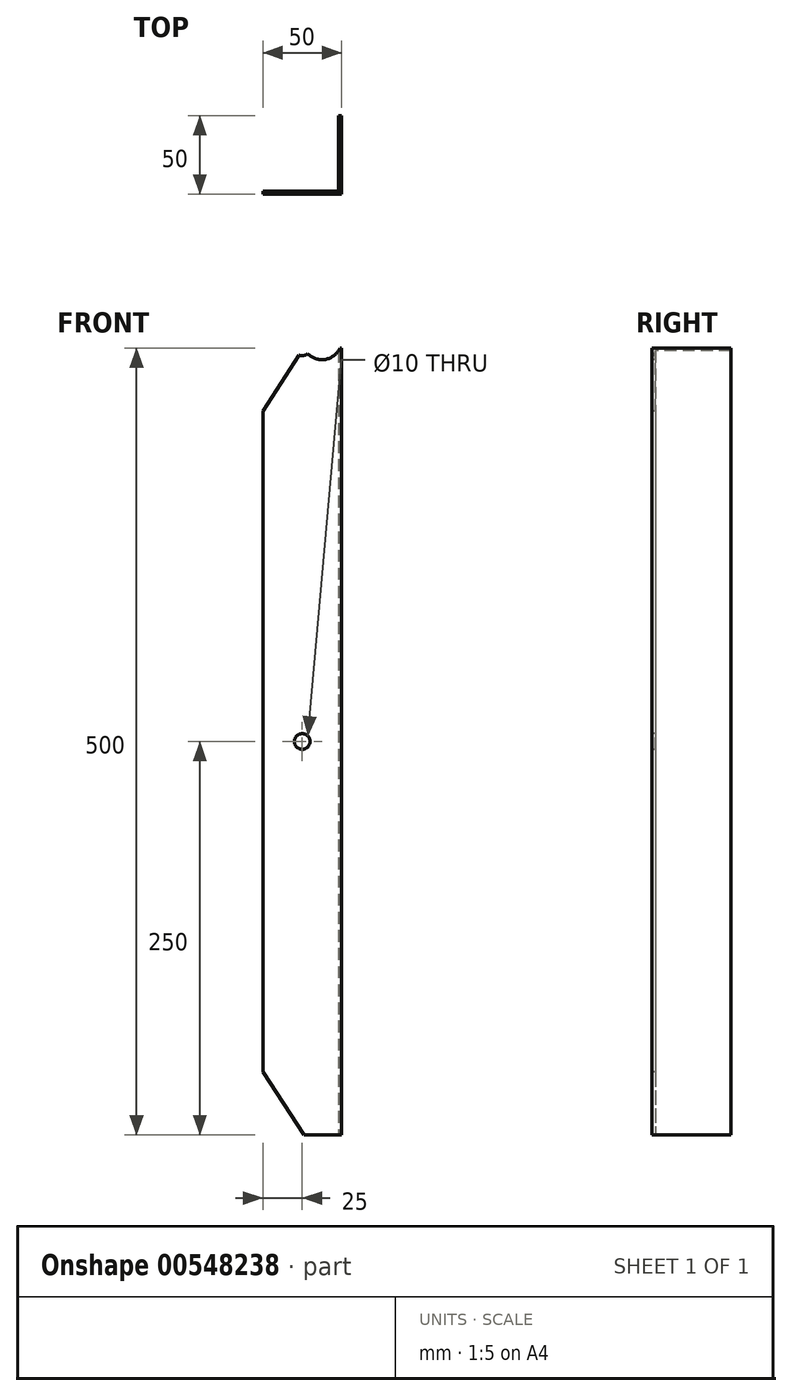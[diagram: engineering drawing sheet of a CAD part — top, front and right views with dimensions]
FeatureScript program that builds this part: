
annotation { "Feature Type Name" : "Feature", "Feature Type Description" : "" }
export const myFeature = defineFeature(function(context is Context, id is Id, definition is map)
    precondition{}
    {
        {
            var Q0;
            Q0=qCreatedBy(makeId("Top.planeOp"),FACE);
            var sketch = newSketch(context, id + "F0", { "sketchPlane" : qUnion([Q0])});
            skLineSegment(sketch, "E0", {"start": v(0, 0) * mm, "end": v(-50, 0) * mm});
            skLineSegment(sketch, "E1", {"start": v(0, 0) * mm, "end": v(0, 50) * mm});
            skLineSegment(sketch, "E2.0", {"start": v(-2, 2) * mm, "end": v(-50, 2) * mm});
            skLineSegment(sketch, "E2.1", {"start": v(-2, 2) * mm, "end": v(-2, 50) * mm});
            skLineSegment(sketch, "E3", {"start": v(-50, 2) * mm, "end": v(-50, 0) * mm});
            skLineSegment(sketch, "E4", {"start": v(-2, 50) * mm, "end": v(0, 50) * mm});
            skSolve(sketch);
        }
        {
            var Q0;
            Q0=makeQuery(id+"F0.imprint","IMPRINT",FACE,{"disambiguationData":[TD([[makeQuery(id+"F0.imprint","IMPRINT",EDGE,{"derivedFrom":sQuery(id+"F0.wireOp",EDGE,"E0")}),-1.0]])]});
            extrude(context, id + "F1", {"entities" : qUnion([Q0]), "depth" : 500 * mm, "offsetDistance" : 25 * mm});
        }
        {
            var Q0;
            Q0=makeQuery(id+"F1.opExtrude","SWEPT_FACE",FACE,{"disambiguationData":[OSD([sQuery(id+"F0.wireOp",EDGE,"E0")])]});
            var sketch = newSketch(context, id + "F2", { "sketchPlane" : qUnion([Q0])});
            skLineSegment(sketch, "E5", {"start": v(-25, 0) * mm, "end": v(-25, 500) * mm});
            skCircle(sketch, "E6", {"center": v(-25, 500) * mm, "radius": 5 * mm});
            skSolve(sketch);
        }
        {
            var Q0;
            Q0=makeQuery(id+"F2.imprint","IMPRINT",FACE,{"disambiguationData":[TD([[makeQuery(id+"F2.imprint","IMPRINT",EDGE,{"derivedFrom":sQuery(id+"F2.wireOp",EDGE,"E6")}),1.0]])]});
            extrude(context, id + "F3", {"entities" : qUnion([Q0]), "operationType" : NewBodyOperationType.REMOVE, "oppositeDirection" : true, "depth" : 25 * mm, "offsetDistance" : 25 * mm});
        }
        {
            var Q0;
            Q0=makeQuery(id+"F1.opExtrude","SWEPT_FACE",FACE,{"disambiguationData":[OSD([sQuery(id+"F0.wireOp",EDGE,"E0")])]});
            var sketch = newSketch(context, id + "F4", { "sketchPlane" : qUnion([Q0])});
            skLineSegment(sketch, "E7", {"start": v(0, 500) * mm, "end": v(-12.5, 500) * mm});
            skLineSegment(sketch, "E8", {"start": v(-12.5, 500) * mm, "end": v(-12.5, 505) * mm});
            skCircle(sketch, "E9", {"center": v(-12.5, 505) * mm, "radius": 12.5 * mm});
            skLineSegment(sketch, "E10", {"start": v(-50, 500) * mm, "end": v(-50, 460) * mm});
            skLineSegment(sketch, "E11", {"start": v(-50, 460) * mm, "end": v(-23.96, 500) * mm});
            skLineSegment(sketch, "E12", {"start": v(-23.96, 500) * mm, "end": v(-50, 500) * mm});
            skLineSegment(sketch, "E13", {"start": v(0, 250) * mm, "end": v(-50, 250) * mm});
            skLineSegment(sketch, "E14.MirrorCS", {"start": v(-50, 0) * mm, "end": v(-50, 40) * mm});
            skLineSegment(sketch, "E15.MirrorCS", {"start": v(-50, 40) * mm, "end": v(-23.96, 0) * mm});
            skLineSegment(sketch, "E16.MirrorCS", {"start": v(-23.96, 0) * mm, "end": v(-50, 0) * mm});
            skCircle(sketch, "E17.MirrorC", {"center": v(-12.5, -5) * mm, "radius": 12.5 * mm});
            skCircle(sketch, "E18", {"center": v(-25, 250) * mm, "radius": 5 * mm});
            skSolve(sketch);
        }
        {
            var Q0;
            {var subQ0=sQuery(id+"F4.wireOp",EDGE,"E7");var subQ1=makeQuery(id+"F1.opExtrude","CAP_EDGE",EDGE,{"disambiguationData":[OSD([sQuery(id+"F0.wireOp",EDGE,"E0")])],"isStart":false});var subQ2=makeQuery(id+"F4.imprint","INTERSECT",VERTEX,{"derivedFrom":[subQ1,subQ0]});Q0=makeQuery(id+"F4.imprint","IMPRINT",FACE,{"disambiguationData":[TD([[makeQuery(id+"F4.imprint","IMPRINT",EDGE,{"disambiguationData":[TD([[subQ2,1.0]])],"derivedFrom":subQ0}),1.0]])]});}
            var Q1;
            Q1=makeQuery(id+"F4.imprint","IMPRINT",FACE,{"disambiguationData":[TD([[makeQuery(id+"F4.imprint","IMPRINT",EDGE,{"derivedFrom":sQuery(id+"F4.wireOp",EDGE,"E10")}),1.0]])]});
            extrude(context, id + "F5", {"entities" : qUnion([Q0, Q1]), "operationType" : NewBodyOperationType.REMOVE, "oppositeDirection" : true, "depth" : 50 * mm, "offsetDistance" : 25 * mm});
        }
        {
            var Q0;
            Q0=makeQuery(id+"F4.imprint","IMPRINT",FACE,{"disambiguationData":[TD([[makeQuery(id+"F4.imprint","IMPRINT",EDGE,{"derivedFrom":sQuery(id+"F4.wireOp",EDGE,"E14.MirrorCS")}),1.0]])]});
            var Q1;
            {var subQ0=sQuery(id+"F4.wireOp",EDGE,"E17.MirrorC");var subQ1=makeQuery(id+"F1.opExtrude","CAP_EDGE",EDGE,{"disambiguationData":[OSD([sQuery(id+"F0.wireOp",EDGE,"E0")])],"isStart":true});var subQ3=makeQuery(id+"F4.imprint","INTERSECT",VERTEX,{"derivedFrom":[subQ1,subQ0]});Q1=makeQuery(id+"F4.imprint","IMPRINT",FACE,{"disambiguationData":[TD([[makeQuery(id+"F4.imprint","IMPRINT",EDGE,{"disambiguationData":[TD([[subQ3,1.0]])],"derivedFrom":subQ0}),-1.0]])]});}
            extrude(context, id + "F6", {"entities" : qUnion([Q0, Q1]), "operationType" : NewBodyOperationType.REMOVE, "oppositeDirection" : true, "depth" : 50 * mm, "offsetDistance" : 25 * mm});
        }
        {
            var Q0;
            {var subQ0=sQuery(id+"F4.wireOp",EDGE,"E18");var subQ1=sQuery(id+"F4.wireOp",EDGE,"E13");var subQ2=makeQuery(id+"F4.imprint","INTERSECT",VERTEX,{"disambiguationData":[OD(0.0)],"derivedFrom":[subQ1,subQ0]});Q0=makeQuery(id+"F4.imprint","IMPRINT",FACE,{"disambiguationData":[TD([[makeQuery(id+"F4.imprint","IMPRINT",EDGE,{"disambiguationData":[TD([[subQ2,-1.0]])],"derivedFrom":subQ1}),1.0]])]});}
            var Q1;
            {var subQ0=sQuery(id+"F4.wireOp",EDGE,"E18");var subQ1=sQuery(id+"F4.wireOp",EDGE,"E13");var subQ2=makeQuery(id+"F4.imprint","INTERSECT",VERTEX,{"disambiguationData":[OD(0.0)],"derivedFrom":[subQ1,subQ0]});Q1=makeQuery(id+"F4.imprint","IMPRINT",FACE,{"disambiguationData":[TD([[makeQuery(id+"F4.imprint","IMPRINT",EDGE,{"disambiguationData":[TD([[subQ2,-1.0]])],"derivedFrom":subQ1}),-1.0]])]});}
            extrude(context, id + "F7", {"entities" : qUnion([Q0, Q1]), "operationType" : NewBodyOperationType.REMOVE, "oppositeDirection" : true, "depth" : 25 * mm, "offsetDistance" : 25 * mm});
        }
    });
